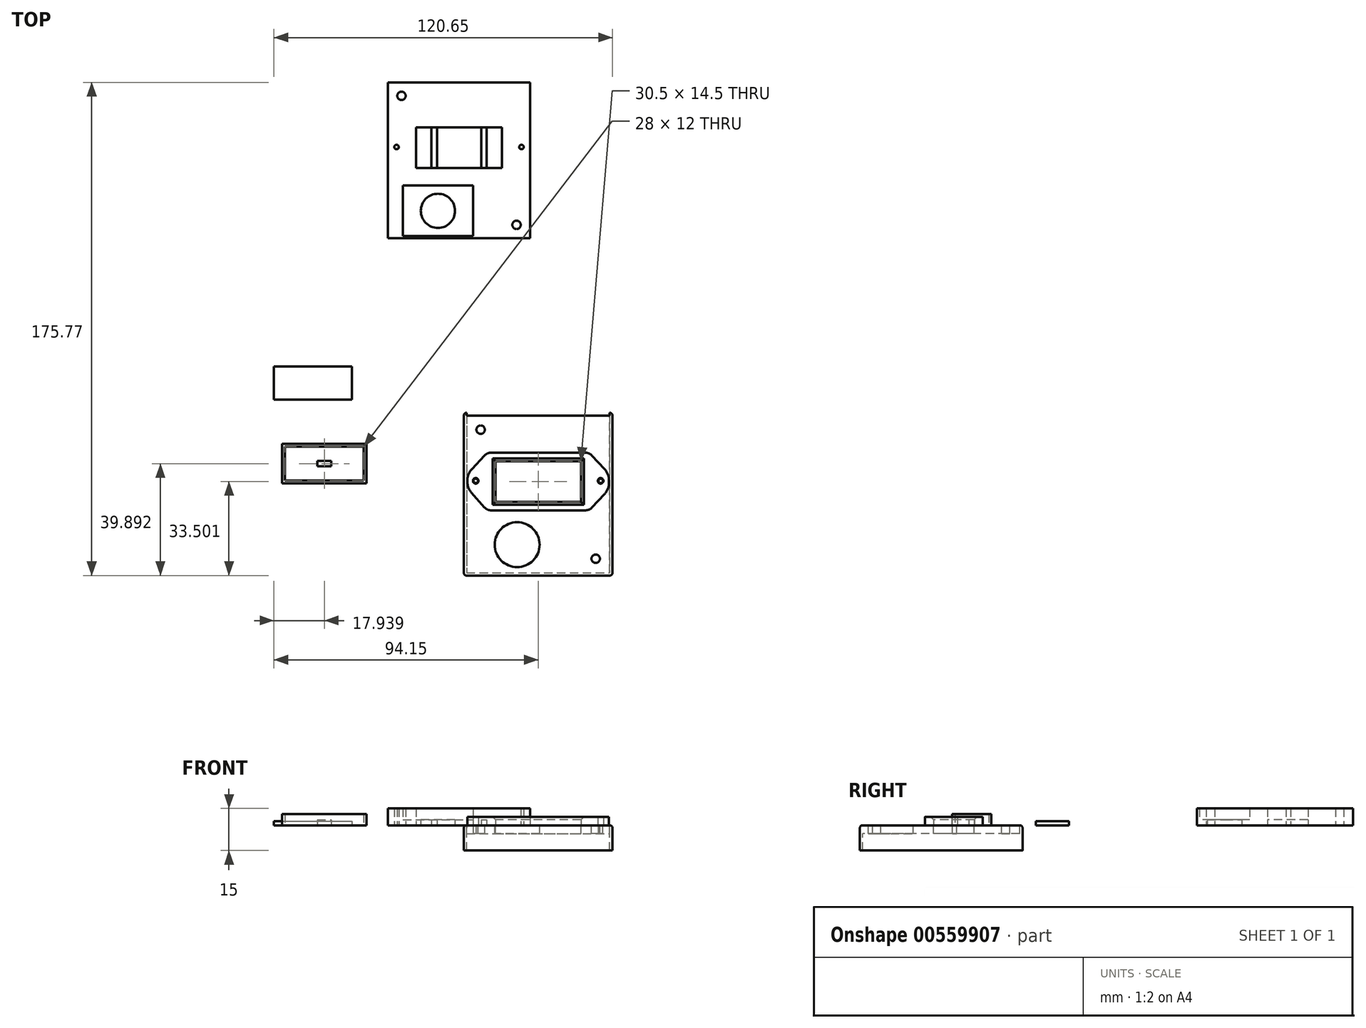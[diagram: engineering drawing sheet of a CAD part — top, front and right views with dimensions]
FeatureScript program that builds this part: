
annotation { "Feature Type Name" : "Feature", "Feature Type Description" : "" }
export const myFeature = defineFeature(function(context is Context, id is Id, definition is map)
    precondition{}
    {
        {
            var Q0;
            Q0=qCreatedBy(makeId("Top.planeOp"),FACE);
            var sketch = newSketch(context, id + "F0", { "sketchPlane" : qUnion([Q0])});
            skLineSegment(sketch, "E0.bottom", {"start": v(25.5, 28) * mm, "end": v(-25.5, 28) * mm});
            skLineSegment(sketch, "E0.top", {"start": v(25.5, -28) * mm, "end": v(-25.5, -28) * mm});
            skLineSegment(sketch, "E0.left", {"start": v(25.5, 28) * mm, "end": v(25.5, -28) * mm});
            skLineSegment(sketch, "E0.right", {"start": v(-25.5, 28) * mm, "end": v(-25.5, -28) * mm});
            skCircle(sketch, "E1", {"center": v(-20.5, 23) * mm, "radius": 1.5 * mm});
            skCircle(sketch, "E2", {"center": v(20.5, -23) * mm, "radius": 1.5 * mm});
            skCircle(sketch, "E3", {"center": v(-7.5, -18) * mm, "radius": 6.1 * mm});
            skLineSegment(sketch, "E4.bottom", {"start": v(-15.25, 11.75) * mm, "end": v(15.25, 11.75) * mm});
            skLineSegment(sketch, "E4.top", {"start": v(-15.25, -2.75) * mm, "end": v(15.25, -2.75) * mm});
            skLineSegment(sketch, "E4.left", {"start": v(-15.25, 11.75) * mm, "end": v(-15.25, -2.75) * mm});
            skLineSegment(sketch, "E4.right", {"start": v(15.25, 11.75) * mm, "end": v(15.25, -2.75) * mm});
            skLineSegment(sketch, "E5.bottom", {"start": v(-2.5, 11.75) * mm, "end": v(2.5, 11.75) * mm});
            skLineSegment(sketch, "E5.top", {"start": v(-2.5, -2.75) * mm, "end": v(2.5, -2.75) * mm});
            skLineSegment(sketch, "E5.left", {"start": v(-2.5, 11.75) * mm, "end": v(-2.5, -2.75) * mm});
            skLineSegment(sketch, "E5.right", {"start": v(2.5, 11.75) * mm, "end": v(2.5, -2.75) * mm});
            skLineSegment(sketch, "E6.bottom", {"start": v(-6.25, 10.5) * mm, "end": v(5.75, 10.5) * mm, "construction": true});
            skLineSegment(sketch, "E6.top", {"start": v(-6.25, -1.5) * mm, "end": v(5.75, -1.5) * mm, "construction": true});
            skLineSegment(sketch, "E6.left", {"start": v(-6.25, 10.5) * mm, "end": v(-6.25, -1.5) * mm, "construction": true});
            skLineSegment(sketch, "E6.right", {"start": v(5.75, 10.5) * mm, "end": v(5.75, -1.5) * mm, "construction": true});
            skLineSegment(sketch, "E7.bottom", {"start": v(-14, 10.5) * mm, "end": v(14, 10.5) * mm, "construction": true});
            skLineSegment(sketch, "E7.top", {"start": v(-14, -1.5) * mm, "end": v(14, -1.5) * mm, "construction": true});
            skLineSegment(sketch, "E7.left", {"start": v(-14, 10.5) * mm, "end": v(-14, -1.5) * mm, "construction": true});
            skLineSegment(sketch, "E7.right", {"start": v(14, 10.5) * mm, "end": v(14, -1.5) * mm, "construction": true});
            skSolve(sketch);
        }
        {
            var Q0;
            Q0=makeQuery(id+"F0.imprint","IMPRINT",FACE,{"disambiguationData":[TD([[makeQuery(id+"F0.imprint","IMPRINT",EDGE,{"derivedFrom":sQuery(id+"F0.wireOp",EDGE,"E0.bottom")}),1.0]])]});
            var Q1;
            Q1=makeQuery(id+"F0.imprint","IMPRINT",FACE,{"disambiguationData":[TD([[makeQuery(id+"F0.imprint","IMPRINT",EDGE,{"derivedFrom":sQuery(id+"F0.wireOp",EDGE,"LN2d2Qam-zQ4N-hJWI-jsZm-hQ2YjQqxJFMe.bottom")}),-1.0]])]});
            var Q2;
            Q2=makeQuery(id+"F0.imprint","IMPRINT",FACE,{"disambiguationData":[TD([[makeQuery(id+"F0.imprint","IMPRINT",EDGE,{"derivedFrom":sQuery(id+"F0.wireOp",EDGE,"Tyq8l7xN-NJ6r-rAiC-5Q4v-MCzvgNdMf9WX.bottom")}),-1.0]])]});
            var Q3;
            Q3=makeQuery(id+"F0.imprint","IMPRINT",FACE,{"disambiguationData":[TD([[makeQuery(id+"F0.imprint","IMPRINT",EDGE,{"derivedFrom":sQuery(id+"F0.wireOp",EDGE,"E5.bottom")}),-1.0]])]});
            var Q4;
            {var subQ12=sQuery(id+"F0.wireOp",EDGE,"5e66b00e-83e9-4da4-8626-02964c2a5a3e.left");Q4=makeQuery(id+"F0.imprint","IMPRINT",FACE,{"disambiguationData":[TD([[makeQuery(id+"F0.imprint","IMPRINT",EDGE,{"derivedFrom":subQ12}),-1.0]])]});}
            var Q5;
            Q5=makeQuery(id+"F0.imprint","IMPRINT",FACE,{"disambiguationData":[TD([[makeQuery(id+"F0.imprint","IMPRINT",EDGE,{"derivedFrom":sQuery(id+"F0.wireOp",EDGE,"242b43d6-e01b-45f4-8fda-c560a832d6e8.bottom")}),-1.0]])]});
            var Q6;
            Q6=makeQuery(id+"F0.imprint","IMPRINT",FACE,{"disambiguationData":[TD([[makeQuery(id+"F0.imprint","IMPRINT",EDGE,{"derivedFrom":sQuery(id+"F0.wireOp",EDGE,"c80b9b78-23ee-44ab-b0c4-abc6401d7a6b.bottom")}),-1.0]])]});
            var Q7;
            Q7=makeQuery(id+"F0.imprint","IMPRINT",FACE,{"disambiguationData":[TD([[makeQuery(id+"F0.imprint","IMPRINT",EDGE,{"derivedFrom":sQuery(id+"F0.wireOp",EDGE,"V3zyF6Pa-9TGi-MSfi-dUwD-Oto6uP0OLka4.bottom")}),-1.0]])]});
            extrude(context, id + "F1", {"entities" : qUnion([Q0, Q1, Q2, Q3, Q4, Q5, Q6, Q7]), "depth" : 1 * mm});
        }
        {
            var Q0;
            Q0=qCreatedBy(makeId("Top.planeOp"),FACE);
            var sketch = newSketch(context, id + "F2", { "sketchPlane" : qUnion([Q0])});
            skPoint(sketch, "E8.middle", {"position": v(28.78, -122.02) * mm});
            skLineSegment(sketch, "E9.bottom", {"start": v(14.21, -108.47) * mm, "end": v(42.21, -108.47) * mm, "construction": true});
            skLineSegment(sketch, "E9.top", {"start": v(14.21, -120.47) * mm, "end": v(42.21, -120.47) * mm, "construction": true});
            skLineSegment(sketch, "E9.left", {"start": v(14.21, -108.47) * mm, "end": v(14.21, -120.47) * mm, "construction": true});
            skLineSegment(sketch, "E9.right", {"start": v(42.21, -108.47) * mm, "end": v(42.21, -120.47) * mm, "construction": true});
            skLineSegment(sketch, "E10.bottom", {"start": v(20.96, -108.47) * mm, "end": v(23.46, -108.47) * mm, "construction": true});
            skLineSegment(sketch, "E10.top", {"start": v(20.96, -120.47) * mm, "end": v(23.46, -120.47) * mm, "construction": true});
            skLineSegment(sketch, "E10.left", {"start": v(20.96, -108.47) * mm, "end": v(20.96, -120.47) * mm, "construction": true});
            skLineSegment(sketch, "E10.right", {"start": v(23.46, -108.47) * mm, "end": v(23.46, -120.47) * mm, "construction": true});
            skLineSegment(sketch, "E11.bottom", {"start": v(32.96, -108.47) * mm, "end": v(35.46, -108.47) * mm, "construction": true});
            skLineSegment(sketch, "E11.top", {"start": v(32.96, -120.47) * mm, "end": v(35.46, -120.47) * mm, "construction": true});
            skLineSegment(sketch, "E11.left", {"start": v(32.96, -108.47) * mm, "end": v(32.96, -120.47) * mm, "construction": true});
            skLineSegment(sketch, "E11.right", {"start": v(35.46, -108.47) * mm, "end": v(35.46, -120.47) * mm, "construction": true});
            skLineSegment(sketch, "E12.bottom", {"start": v(19.21, -111.47) * mm, "end": v(25.21, -111.47) * mm, "construction": true});
            skLineSegment(sketch, "E12.top", {"start": v(19.21, -117.47) * mm, "end": v(25.21, -117.47) * mm, "construction": true});
            skLineSegment(sketch, "E12.left", {"start": v(19.21, -111.47) * mm, "end": v(19.21, -117.47) * mm, "construction": true});
            skLineSegment(sketch, "E12.right", {"start": v(25.21, -111.47) * mm, "end": v(25.21, -117.47) * mm, "construction": true});
            skLineSegment(sketch, "E13.bottom", {"start": v(31.21, -111.47) * mm, "end": v(37.21, -111.47) * mm, "construction": true});
            skLineSegment(sketch, "E13.top", {"start": v(31.21, -117.47) * mm, "end": v(37.21, -117.47) * mm, "construction": true});
            skLineSegment(sketch, "E13.left", {"start": v(31.21, -111.47) * mm, "end": v(31.21, -117.47) * mm, "construction": true});
            skLineSegment(sketch, "E13.right", {"start": v(37.21, -111.47) * mm, "end": v(37.21, -117.47) * mm, "construction": true});
            skLineSegment(sketch, "E14.bottom", {"start": v(2.71, -90.97) * mm, "end": v(53.71, -90.97) * mm});
            skLineSegment(sketch, "E14.top", {"start": v(2.71, -146.97) * mm, "end": v(53.71, -146.97) * mm});
            skLineSegment(sketch, "E14.left", {"start": v(2.71, -90.97) * mm, "end": v(2.71, -146.97) * mm});
            skLineSegment(sketch, "E14.right", {"start": v(53.71, -90.97) * mm, "end": v(53.71, -146.97) * mm});
            skCircle(sketch, "E15", {"center": v(7.71, -95.97) * mm, "radius": 1.5 * mm});
            skCircle(sketch, "E16", {"center": v(48.71, -141.97) * mm, "radius": 1.5 * mm});
            skCircle(sketch, "E17", {"center": v(20.71, -136.97) * mm, "radius": 8 * mm});
            skLineSegment(sketch, "E18.bottom", {"start": v(12.96, -107.22) * mm, "end": v(43.46, -107.22) * mm});
            skLineSegment(sketch, "E18.top", {"start": v(12.96, -121.72) * mm, "end": v(43.46, -121.72) * mm});
            skLineSegment(sketch, "E18.left", {"start": v(12.96, -107.22) * mm, "end": v(12.96, -121.72) * mm});
            skLineSegment(sketch, "E18.right", {"start": v(43.46, -107.22) * mm, "end": v(43.46, -121.72) * mm});
            skPoint(sketch, "E19.middle", {"position": v(-49.22, -118.43) * mm});
            skLineSegment(sketch, "E20.bottom", {"start": v(-62, -102.08) * mm, "end": v(-34, -102.08) * mm});
            skLineSegment(sketch, "E20.top", {"start": v(-62, -114.08) * mm, "end": v(-34, -114.08) * mm});
            skLineSegment(sketch, "E20.left", {"start": v(-62, -102.08) * mm, "end": v(-62, -114.08) * mm});
            skLineSegment(sketch, "E20.right", {"start": v(-34, -102.08) * mm, "end": v(-34, -114.08) * mm});
            skLineSegment(sketch, "E21.bottom", {"start": v(-54.75, -102.08) * mm, "end": v(-52.25, -102.08) * mm, "construction": true});
            skLineSegment(sketch, "E21.top", {"start": v(-54.75, -114.08) * mm, "end": v(-52.25, -114.08) * mm, "construction": true});
            skLineSegment(sketch, "E21.left", {"start": v(-54.75, -102.08) * mm, "end": v(-54.75, -114.08) * mm, "construction": true});
            skLineSegment(sketch, "E21.right", {"start": v(-52.25, -102.08) * mm, "end": v(-52.25, -114.08) * mm, "construction": true});
            skLineSegment(sketch, "E22.bottom", {"start": v(-43.75, -102.08) * mm, "end": v(-41.25, -102.08) * mm, "construction": true});
            skLineSegment(sketch, "E22.top", {"start": v(-43.75, -114.08) * mm, "end": v(-41.25, -114.08) * mm, "construction": true});
            skLineSegment(sketch, "E22.left", {"start": v(-43.75, -102.08) * mm, "end": v(-43.75, -114.08) * mm, "construction": true});
            skLineSegment(sketch, "E22.right", {"start": v(-41.25, -102.08) * mm, "end": v(-41.25, -114.08) * mm, "construction": true});
            skLineSegment(sketch, "E23.bottom", {"start": v(-56.5, -105.08) * mm, "end": v(-50.5, -105.08) * mm, "construction": true});
            skLineSegment(sketch, "E23.top", {"start": v(-56.5, -111.08) * mm, "end": v(-50.5, -111.08) * mm, "construction": true});
            skLineSegment(sketch, "E23.left", {"start": v(-56.5, -105.08) * mm, "end": v(-56.5, -111.08) * mm, "construction": true});
            skLineSegment(sketch, "E23.right", {"start": v(-50.5, -105.08) * mm, "end": v(-50.5, -111.08) * mm, "construction": true});
            skLineSegment(sketch, "E24.bottom", {"start": v(-45.5, -105.08) * mm, "end": v(-39.5, -105.08) * mm, "construction": true});
            skLineSegment(sketch, "E24.top", {"start": v(-45.5, -111.08) * mm, "end": v(-39.5, -111.08) * mm, "construction": true});
            skLineSegment(sketch, "E24.left", {"start": v(-45.5, -105.08) * mm, "end": v(-45.5, -111.08) * mm, "construction": true});
            skLineSegment(sketch, "E24.right", {"start": v(-39.5, -105.08) * mm, "end": v(-39.5, -111.08) * mm, "construction": true});
            skLineSegment(sketch, "E25.bottom", {"start": v(-63, -101.08) * mm, "end": v(-33, -101.08) * mm});
            skLineSegment(sketch, "E25.top", {"start": v(-63, -115.08) * mm, "end": v(-33, -115.08) * mm});
            skLineSegment(sketch, "E25.left", {"start": v(-63, -101.08) * mm, "end": v(-63, -115.08) * mm});
            skLineSegment(sketch, "E25.right", {"start": v(-33, -101.08) * mm, "end": v(-33, -115.08) * mm});
            skLineSegment(sketch, "E26.bottom", {"start": v(-50.5, -107.08) * mm, "end": v(-45.5, -107.08) * mm});
            skLineSegment(sketch, "E26.right", {"start": v(-34, -107.08) * mm, "end": v(-34, -109.08) * mm});
            skLineSegment(sketch, "E27.bottom", {"start": v(-50.5, -102.08) * mm, "end": v(-45.5, -102.08) * mm});
            skLineSegment(sketch, "E27.top", {"start": v(-50.5, -114.08) * mm, "end": v(-45.5, -114.08) * mm});
            skLineSegment(sketch, "E27.left", {"start": v(-50.5, -102.08) * mm, "end": v(-50.5, -114.08) * mm});
            skLineSegment(sketch, "E27.right", {"start": v(-45.5, -102.08) * mm, "end": v(-45.5, -114.08) * mm});
            skLineSegment(sketch, "E28.top", {"start": v(2.71, -89.97) * mm, "end": v(53.71, -89.97) * mm});
            skLineSegment(sketch, "E28.left", {"start": v(2.71, -90.97) * mm, "end": v(2.71, -89.97) * mm});
            skLineSegment(sketch, "E28.right", {"start": v(53.71, -90.97) * mm, "end": v(53.71, -89.97) * mm});
            skLineSegment(sketch, "E29.top", {"start": v(2.71, -147.97) * mm, "end": v(53.71, -147.97) * mm});
            skLineSegment(sketch, "E29.left", {"start": v(2.71, -146.97) * mm, "end": v(2.71, -147.97) * mm});
            skLineSegment(sketch, "E29.right", {"start": v(53.71, -146.97) * mm, "end": v(53.71, -147.97) * mm});
            skLineSegment(sketch, "E30.bottom", {"start": v(53.71, -89.97) * mm, "end": v(54.71, -89.97) * mm});
            skLineSegment(sketch, "E30.top", {"start": v(53.71, -147.97) * mm, "end": v(54.71, -147.97) * mm});
            skLineSegment(sketch, "E30.left", {"start": v(53.71, -89.97) * mm, "end": v(53.71, -147.97) * mm});
            skLineSegment(sketch, "E30.right", {"start": v(54.71, -89.97) * mm, "end": v(54.71, -147.97) * mm});
            skLineSegment(sketch, "E31.bottom", {"start": v(2.71, -89.97) * mm, "end": v(1.71, -89.97) * mm});
            skLineSegment(sketch, "E31.top", {"start": v(2.71, -147.97) * mm, "end": v(1.71, -147.97) * mm});
            skLineSegment(sketch, "E31.left", {"start": v(2.71, -89.97) * mm, "end": v(2.71, -147.97) * mm});
            skLineSegment(sketch, "E31.right", {"start": v(1.71, -89.97) * mm, "end": v(1.71, -147.97) * mm});
            skCircle(sketch, "E32", {"center": v(5.96, -114.22) * mm, "radius": 0.8 * mm});
            skCircle(sketch, "E33", {"center": v(50.46, -114.22) * mm, "radius": 0.8 * mm});
            skLineSegment(sketch, "E34.trimOffspring", {"start": v(-50.5, -109.08) * mm, "end": v(-45.5, -109.08) * mm});
            skSolve(sketch);
        }
        {
            var Q0;
            Q0=qCreatedBy(makeId("Top.planeOp"),FACE);
            var sketch = newSketch(context, id + "F3", { "sketchPlane" : qUnion([Q0])});
            skLineSegment(sketch, "E35.bottom", {"start": v(-65.94, -73.47) * mm, "end": v(-38.14, -73.47) * mm});
            skLineSegment(sketch, "E35.top", {"start": v(-65.94, -85.27) * mm, "end": v(-38.14, -85.27) * mm});
            skLineSegment(sketch, "E35.left", {"start": v(-65.94, -73.47) * mm, "end": v(-65.94, -85.27) * mm});
            skLineSegment(sketch, "E35.right", {"start": v(-38.14, -73.47) * mm, "end": v(-38.14, -85.27) * mm});
            skSolve(sketch);
        }
        {
            var Q0;
            Q0=makeQuery(id+"F1.opExtrude","CAP_FACE",FACE,{"disambiguationData":[OSD([sQuery(id+"F0.wireOp",EDGE,"E0.bottom"),sQuery(id+"F0.wireOp",EDGE,"E0.top"),sQuery(id+"F0.wireOp",EDGE,"E0.left"),sQuery(id+"F0.wireOp",EDGE,"E0.right"),sQuery(id+"F0.wireOp",EDGE,"E1"),sQuery(id+"F0.wireOp",EDGE,"E2"),sQuery(id+"F0.wireOp",EDGE,"E3"),sQuery(id+"F0.wireOp",EDGE,"E4.bottom"),sQuery(id+"F0.wireOp",EDGE,"E4.top"),sQuery(id+"F0.wireOp",EDGE,"E4.left"),sQuery(id+"F0.wireOp",EDGE,"E4.right"),sQuery(id+"F0.wireOp",EDGE,"E5.left"),sQuery(id+"F0.wireOp",EDGE,"E5.right")])],"isStart":false});
            var sketch = newSketch(context, id + "F4", { "sketchPlane" : qUnion([Q0])});
            skLineSegment(sketch, "E36.bottom", {"start": v(-6.25, 10.25) * mm, "end": v(5.75, 10.25) * mm, "construction": true});
            skLineSegment(sketch, "E36.top", {"start": v(-6.25, -1.75) * mm, "end": v(5.75, -1.75) * mm, "construction": true});
            skLineSegment(sketch, "E36.left", {"start": v(-6.25, 10.25) * mm, "end": v(-6.25, -1.75) * mm, "construction": true});
            skLineSegment(sketch, "E36.right", {"start": v(5.75, 10.25) * mm, "end": v(5.75, -1.75) * mm, "construction": true});
            skSolve(sketch);
        }
        {
            var Q0;
            {var subQ3=sQuery(id+"F2.wireOp",EDGE,"E20.left");Q0=makeQuery(id+"F2.imprint","IMPRINT",FACE,{"disambiguationData":[TD([[makeQuery(id+"F2.imprint","IMPRINT",EDGE,{"derivedFrom":subQ3}),-1.0]])]});}
            extrude(context, id + "F5", {"entities" : qUnion([Q0]), "depth" : 4 * mm});
        }
        {
            var Q0;
            Q0=makeQuery(id+"F2.imprint","IMPRINT",FACE,{"disambiguationData":[TD([[makeQuery(id+"F2.imprint","IMPRINT",EDGE,{"derivedFrom":sQuery(id+"F2.wireOp",EDGE,"E15")}),-1.0]])]});
            extrude(context, id + "F6", {"entities" : qUnion([Q0]), "oppositeDirection" : true, "depth" : 3 * mm});
        }
        {
            var Q0;
            Q0=makeQuery(id+"F2.imprint","IMPRINT",FACE,{"disambiguationData":[TD([[makeQuery(id+"F2.imprint","IMPRINT",EDGE,{"derivedFrom":sQuery(id+"F2.wireOp",EDGE,"E26.bottom")}),-1.0]])]});
            var Q1;
            {var subQ5=sQuery(id+"F2.wireOp",EDGE,"E27.bottom");Q1=makeQuery(id+"F2.imprint","IMPRINT",FACE,{"disambiguationData":[TD([[makeQuery(id+"F2.imprint","IMPRINT",EDGE,{"derivedFrom":subQ5}),-1.0]])]});}
            var Q2;
            {var subQ5=sQuery(id+"F2.wireOp",EDGE,"E27.top");Q2=makeQuery(id+"F2.imprint","IMPRINT",FACE,{"disambiguationData":[TD([[makeQuery(id+"F2.imprint","IMPRINT",EDGE,{"derivedFrom":subQ5}),1.0]])]});}
            extrude(context, id + "F7", {"entities" : qUnion([Q0, Q1, Q2]), "operationType" : NewBodyOperationType.ADD, "depth" : 2 * mm});
        }
        {
            var Q0;
            Q0=makeQuery(id+"F3.imprint","IMPRINT",FACE,{"disambiguationData":[TD([[makeQuery(id+"F3.imprint","IMPRINT",EDGE,{"derivedFrom":sQuery(id+"F3.wireOp",EDGE,"E35.bottom")}),-1.0]])]});
            extrude(context, id + "F8", {"entities" : qUnion([Q0]), "depth" : 1.5 * mm});
        }
        {
            var Q0;
            {var subQ3=sQuery(id+"F2.wireOp",EDGE,"E31.bottom");Q0=makeQuery(id+"F2.imprint","IMPRINT",FACE,{"disambiguationData":[TD([[makeQuery(id+"F2.imprint","IMPRINT",EDGE,{"derivedFrom":subQ3}),1.0]])]});}
            var Q1;
            {var subQ0=sQuery(id+"F2.wireOp",EDGE,"E14.bottom");Q1=makeQuery(id+"F2.imprint","IMPRINT",FACE,{"disambiguationData":[TD([[makeQuery(id+"F2.imprint","IMPRINT",EDGE,{"derivedFrom":subQ0}),1.0]])]});}
            var Q2;
            {var subQ0=sQuery(id+"F2.wireOp",EDGE,"E14.top");Q2=makeQuery(id+"F2.imprint","IMPRINT",FACE,{"disambiguationData":[TD([[makeQuery(id+"F2.imprint","IMPRINT",EDGE,{"derivedFrom":subQ0}),-1.0]])]});}
            var Q3;
            {var subQ3=sQuery(id+"F2.wireOp",EDGE,"E30.bottom");Q3=makeQuery(id+"F2.imprint","IMPRINT",FACE,{"disambiguationData":[TD([[makeQuery(id+"F2.imprint","IMPRINT",EDGE,{"derivedFrom":subQ3}),-1.0]])]});}
            extrude(context, id + "F9", {"entities" : qUnion([Q0, Q1, Q2, Q3]), "operationType" : NewBodyOperationType.ADD, "oppositeDirection" : true, "depth" : 9 * mm});
        }
        {
            var Q0;
            Q0=makeQuery(id+"F2.imprint","IMPRINT",FACE,{"disambiguationData":[TD([[makeQuery(id+"F2.imprint","IMPRINT",EDGE,{"derivedFrom":sQuery(id+"F2.wireOp",EDGE,"E15")}),-1.0]])]});
            var sketch = newSketch(context, id + "F10", { "sketchPlane" : qUnion([Q0])});
            skLineSegment(sketch, "E37.bottom", {"start": v(9.96, -104.22) * mm, "end": v(46.46, -104.22) * mm});
            skLineSegment(sketch, "E37.top", {"start": v(9.96, -124.72) * mm, "end": v(46.46, -124.72) * mm});
            skLineSegment(sketch, "E37.left", {"start": v(9.96, -104.22) * mm, "end": v(9.96, -124.72) * mm});
            skLineSegment(sketch, "E37.right", {"start": v(46.46, -104.22) * mm, "end": v(46.46, -124.72) * mm});
            skLineSegment(sketch, "E38", {"start": v(9.96, -124.72) * mm, "end": v(2.96, -116.72) * mm});
            skLineSegment(sketch, "E39", {"start": v(2.96, -116.72) * mm, "end": v(2.96, -111.72) * mm});
            skLineSegment(sketch, "E40", {"start": v(2.96, -111.72) * mm, "end": v(9.96, -104.22) * mm});
            skCircle(sketch, "E41", {"center": v(5.96, -114.22) * mm, "radius": 1 * mm});
            skLineSegment(sketch, "E42.bottom", {"start": v(12.96, -107.22) * mm, "end": v(43.46, -107.22) * mm});
            skLineSegment(sketch, "E42.top", {"start": v(12.96, -121.72) * mm, "end": v(43.46, -121.72) * mm});
            skLineSegment(sketch, "E42.left", {"start": v(12.96, -107.22) * mm, "end": v(12.96, -121.72) * mm});
            skLineSegment(sketch, "E42.right", {"start": v(43.46, -107.22) * mm, "end": v(43.46, -121.72) * mm});
            skLineSegment(sketch, "E43", {"start": v(46.46, -104.22) * mm, "end": v(53.46, -111.72) * mm});
            skLineSegment(sketch, "E44", {"start": v(53.46, -111.72) * mm, "end": v(53.46, -117.22) * mm});
            skLineSegment(sketch, "E45", {"start": v(53.46, -117.22) * mm, "end": v(46.46, -124.72) * mm});
            skCircle(sketch, "E46", {"center": v(50.46, -114.22) * mm, "radius": 1 * mm});
            skSolve(sketch);
        }
        {
            var Q0;
            Q0=qSketchRegion(id+"F10",true);
            extrude(context, id + "F11", {"entities" : qUnion([Q0]), "depth" : 3 * mm});
        }
        {
            var Q0;
            Q0=makeQuery(id+"F11.opExtrude","SWEPT_EDGE",EDGE,{"disambiguationData":[OSD([sQuery(id+"F10.wireOp",EDGE,"E39"),sQuery(id+"F10.wireOp",EDGE,"E40")])]});
            var Q1;
            Q1=makeQuery(id+"F11.opExtrude","SWEPT_EDGE",EDGE,{"disambiguationData":[OSD([sQuery(id+"F10.wireOp",EDGE,"E38"),sQuery(id+"F10.wireOp",EDGE,"E39")])]});
            var Q2;
            Q2=makeQuery(id+"F11.opExtrude","SWEPT_EDGE",EDGE,{"disambiguationData":[OSD([sQuery(id+"F10.wireOp",EDGE,"E44"),sQuery(id+"F10.wireOp",EDGE,"E45")])]});
            var Q3;
            Q3=makeQuery(id+"F11.opExtrude","SWEPT_EDGE",EDGE,{"disambiguationData":[OSD([sQuery(id+"F10.wireOp",EDGE,"E43"),sQuery(id+"F10.wireOp",EDGE,"E44")])]});
            fillet(context, id + "F12", {"entities" : qUnion([Q0, Q1, Q2, Q3]), "radius" : 6 * mm, "tangentPropagation" : true, "allowEdgeOverflow" : false});
        }
        {
            var Q0;
            Q0=makeQuery(id+"F11.opExtrude","SWEPT_EDGE",EDGE,{"disambiguationData":[OSD([sQuery(id+"F10.wireOp",EDGE,"E37.bottom"),sQuery(id+"F10.wireOp",EDGE,"E37.left"),sQuery(id+"F10.wireOp",EDGE,"E40")])]});
            var Q1;
            Q1=makeQuery(id+"F11.opExtrude","SWEPT_EDGE",EDGE,{"disambiguationData":[OSD([sQuery(id+"F10.wireOp",EDGE,"E37.top"),sQuery(id+"F10.wireOp",EDGE,"E37.left"),sQuery(id+"F10.wireOp",EDGE,"E38")])]});
            var Q2;
            Q2=makeQuery(id+"F11.opExtrude","SWEPT_EDGE",EDGE,{"disambiguationData":[OSD([sQuery(id+"F10.wireOp",EDGE,"E37.top"),sQuery(id+"F10.wireOp",EDGE,"E37.right"),sQuery(id+"F10.wireOp",EDGE,"E45")])]});
            var Q3;
            Q3=makeQuery(id+"F11.opExtrude","SWEPT_EDGE",EDGE,{"disambiguationData":[OSD([sQuery(id+"F10.wireOp",EDGE,"E37.bottom"),sQuery(id+"F10.wireOp",EDGE,"E37.right"),sQuery(id+"F10.wireOp",EDGE,"E43")])]});
            fillet(context, id + "F13", {"entities" : qUnion([Q0, Q1, Q2, Q3]), "radius" : 3 * mm, "tangentPropagation" : true, "allowEdgeOverflow" : false});
        }
        {
            var Q0;
            Q0=makeQuery(id+"F9.opExtrude","CAP_EDGE",EDGE,{"disambiguationData":[OSD([sQuery(id+"F2.wireOp",EDGE,"E31.right")])],"isStart":true});
            var Q1;
            Q1=makeQuery(id+"F9.opExtrude","CAP_EDGE",EDGE,{"disambiguationData":[OSD([sQuery(id+"F2.wireOp",EDGE,"E28.top"),sQuery(id+"F2.wireOp",EDGE,"E30.bottom"),sQuery(id+"F2.wireOp",EDGE,"E31.bottom")])],"isStart":true});
            var Q2;
            Q2=makeQuery(id+"F9.opExtrude","CAP_EDGE",EDGE,{"disambiguationData":[OSD([sQuery(id+"F2.wireOp",EDGE,"E29.top"),sQuery(id+"F2.wireOp",EDGE,"E30.top"),sQuery(id+"F2.wireOp",EDGE,"E31.top")])],"isStart":true});
            var Q3;
            Q3=makeQuery(id+"F9.opExtrude","CAP_EDGE",EDGE,{"disambiguationData":[OSD([sQuery(id+"F2.wireOp",EDGE,"E30.right")])],"isStart":true});
            var Q4;
            Q4=makeQuery(id+"F9.opExtrude","SWEPT_EDGE",EDGE,{"disambiguationData":[OSD([sQuery(id+"F2.wireOp",EDGE,"E30.top"),sQuery(id+"F2.wireOp",EDGE,"E30.right")])]});
            var Q5;
            Q5=makeQuery(id+"F9.opExtrude","SWEPT_EDGE",EDGE,{"disambiguationData":[OSD([sQuery(id+"F2.wireOp",EDGE,"E31.top"),sQuery(id+"F2.wireOp",EDGE,"E31.right")])]});
            var Q6;
            Q6=makeQuery(id+"F9.opExtrude","SWEPT_EDGE",EDGE,{"disambiguationData":[OSD([sQuery(id+"F2.wireOp",EDGE,"E31.bottom"),sQuery(id+"F2.wireOp",EDGE,"E31.right")])]});
            var Q7;
            Q7=makeQuery(id+"F9.opExtrude","SWEPT_EDGE",EDGE,{"disambiguationData":[OSD([sQuery(id+"F2.wireOp",EDGE,"E30.bottom"),sQuery(id+"F2.wireOp",EDGE,"E30.right")])]});
            fillet(context, id + "F14", {"entities" : qUnion([Q0, Q1, Q2, Q3, Q4, Q5, Q6, Q7]), "radius" : 1 * mm, "tangentPropagation" : true, "allowEdgeOverflow" : false});
        }
        {
            var Q0;
            Q0=makeQuery(id+"F11.opExtrude","CAP_EDGE",EDGE,{"disambiguationData":[OSD([sQuery(id+"F10.wireOp",EDGE,"E42.left")])],"isStart":false});
            var Q1;
            Q1=makeQuery(id+"F11.opExtrude","CAP_EDGE",EDGE,{"disambiguationData":[OSD([sQuery(id+"F10.wireOp",EDGE,"E42.bottom")])],"isStart":false});
            var Q2;
            Q2=makeQuery(id+"F11.opExtrude","CAP_EDGE",EDGE,{"disambiguationData":[OSD([sQuery(id+"F10.wireOp",EDGE,"E42.right")])],"isStart":false});
            var Q3;
            Q3=makeQuery(id+"F11.opExtrude","CAP_EDGE",EDGE,{"disambiguationData":[OSD([sQuery(id+"F10.wireOp",EDGE,"E42.top")])],"isStart":false});
            chamfer(context, id + "F15", {"entities" : qUnion([Q0, Q1, Q2, Q3]), "width" : 1 * mm, "tangentPropagation" : true});
        }
        {
            var Q0;
            Q0=makeQuery(id+"F1.opExtrude","CAP_FACE",FACE,{"disambiguationData":[OSD([sQuery(id+"F0.wireOp",EDGE,"E0.bottom"),sQuery(id+"F0.wireOp",EDGE,"E0.top"),sQuery(id+"F0.wireOp",EDGE,"E0.left"),sQuery(id+"F0.wireOp",EDGE,"E0.right"),sQuery(id+"F0.wireOp",EDGE,"E1"),sQuery(id+"F0.wireOp",EDGE,"E2"),sQuery(id+"F0.wireOp",EDGE,"E3"),sQuery(id+"F0.wireOp",EDGE,"E4.bottom"),sQuery(id+"F0.wireOp",EDGE,"E4.top"),sQuery(id+"F0.wireOp",EDGE,"E4.left"),sQuery(id+"F0.wireOp",EDGE,"E4.right"),sQuery(id+"F0.wireOp",EDGE,"E5.left"),sQuery(id+"F0.wireOp",EDGE,"E5.right")])],"isStart":false});
            var sketch = newSketch(context, id + "F16", { "sketchPlane" : qUnion([Q0])});
            skCircle(sketch, "E47", {"center": v(-20.5, 23) * mm, "radius": 1.5 * mm});
            skCircle(sketch, "E48", {"center": v(20.5, -23) * mm, "radius": 1.5 * mm});
            skCircle(sketch, "E49", {"center": v(-7.5, -18) * mm, "radius": 8.5 * mm, "construction": true});
            skLineSegment(sketch, "E50.bottom", {"start": v(-25.5, 28) * mm, "end": v(25.5, 28) * mm});
            skLineSegment(sketch, "E50.top", {"start": v(-25.5, -28) * mm, "end": v(25.5, -28) * mm});
            skLineSegment(sketch, "E50.left", {"start": v(-25.5, 28) * mm, "end": v(-25.5, -28) * mm});
            skLineSegment(sketch, "E50.right", {"start": v(25.5, 28) * mm, "end": v(25.5, -28) * mm});
            skLineSegment(sketch, "E51.bottom", {"start": v(-15.25, 11.75) * mm, "end": v(15.25, 11.75) * mm});
            skLineSegment(sketch, "E51.top", {"start": v(-15.25, -2.75) * mm, "end": v(15.25, -2.75) * mm});
            skLineSegment(sketch, "E51.left", {"start": v(-15.25, 11.75) * mm, "end": v(-15.25, -2.75) * mm});
            skLineSegment(sketch, "E51.right", {"start": v(15.25, 11.75) * mm, "end": v(15.25, -2.75) * mm});
            skCircle(sketch, "E52", {"center": v(-22.25, 4.75) * mm, "radius": 2 * mm, "construction": true});
            skCircle(sketch, "E53", {"center": v(22.25, 4.75) * mm, "radius": 2 * mm, "construction": true});
            skLineSegment(sketch, "E54.bottom", {"start": v(5, -27) * mm, "end": v(-20, -27) * mm});
            skLineSegment(sketch, "E54.top", {"start": v(5, -9) * mm, "end": v(-20, -9) * mm});
            skLineSegment(sketch, "E54.left", {"start": v(5, -27) * mm, "end": v(5, -9) * mm});
            skLineSegment(sketch, "E54.right", {"start": v(-20, -27) * mm, "end": v(-20, -9) * mm});
            skSolve(sketch);
        }
        {
            var Q0;
            Q0=makeQuery(id+"F5.opExtrude","CAP_FACE",FACE,{"disambiguationData":[OSD([sQuery(id+"F2.wireOp",EDGE,"E20.bottom"),sQuery(id+"F2.wireOp",EDGE,"E20.top"),sQuery(id+"F2.wireOp",EDGE,"E20.left"),sQuery(id+"F2.wireOp",EDGE,"E20.right"),sQuery(id+"F2.wireOp",EDGE,"E25.bottom"),sQuery(id+"F2.wireOp",EDGE,"E25.top"),sQuery(id+"F2.wireOp",EDGE,"E25.left"),sQuery(id+"F2.wireOp",EDGE,"E25.right"),sQuery(id+"F2.wireOp",EDGE,"E26.left"),sQuery(id+"F2.wireOp",EDGE,"E26.right"),sQuery(id+"F2.wireOp",EDGE,"E27.bottom"),sQuery(id+"F2.wireOp",EDGE,"E27.top")])],"isStart":false});
            var sketch = newSketch(context, id + "F17", { "sketchPlane" : qUnion([Q0])});
            skLineSegment(sketch, "E55.bottom", {"start": v(-63, -101.08) * mm, "end": v(-50.5, -101.08) * mm});
            skLineSegment(sketch, "E55.top", {"start": v(-63, -102.08) * mm, "end": v(-50.5, -102.08) * mm});
            skLineSegment(sketch, "E55.left", {"start": v(-63, -101.08) * mm, "end": v(-63, -102.08) * mm});
            skLineSegment(sketch, "E55.right", {"start": v(-50.5, -101.08) * mm, "end": v(-50.5, -102.08) * mm});
            skLineSegment(sketch, "E56.bottom", {"start": v(-63, -102.08) * mm, "end": v(-62, -102.08) * mm});
            skLineSegment(sketch, "E56.top", {"start": v(-63, -115.08) * mm, "end": v(-62, -115.08) * mm});
            skLineSegment(sketch, "E56.left", {"start": v(-63, -102.08) * mm, "end": v(-63, -115.08) * mm});
            skLineSegment(sketch, "E56.right", {"start": v(-62, -102.08) * mm, "end": v(-62, -115.08) * mm});
            skLineSegment(sketch, "E57.bottom", {"start": v(-50.5, -114.08) * mm, "end": v(-62, -114.08) * mm});
            skLineSegment(sketch, "E57.top", {"start": v(-50.5, -115.08) * mm, "end": v(-62, -115.08) * mm});
            skLineSegment(sketch, "E57.left", {"start": v(-50.5, -114.08) * mm, "end": v(-50.5, -115.08) * mm});
            skLineSegment(sketch, "E57.right", {"start": v(-62, -114.08) * mm, "end": v(-62, -115.08) * mm});
            skLineSegment(sketch, "E58.bottom", {"start": v(-33, -101.08) * mm, "end": v(-45.5, -101.08) * mm});
            skLineSegment(sketch, "E58.top", {"start": v(-33, -102.08) * mm, "end": v(-45.5, -102.08) * mm});
            skLineSegment(sketch, "E58.left", {"start": v(-33, -101.08) * mm, "end": v(-33, -102.08) * mm});
            skLineSegment(sketch, "E58.right", {"start": v(-45.5, -101.08) * mm, "end": v(-45.5, -102.08) * mm});
            skLineSegment(sketch, "E59.bottom", {"start": v(-33, -102.08) * mm, "end": v(-34, -102.08) * mm});
            skLineSegment(sketch, "E59.top", {"start": v(-33, -115.08) * mm, "end": v(-34, -115.08) * mm});
            skLineSegment(sketch, "E59.left", {"start": v(-33, -102.08) * mm, "end": v(-33, -115.08) * mm});
            skLineSegment(sketch, "E59.right", {"start": v(-34, -102.08) * mm, "end": v(-34, -115.08) * mm});
            skLineSegment(sketch, "E60.bottom", {"start": v(-45.5, -114.08) * mm, "end": v(-34, -114.08) * mm});
            skLineSegment(sketch, "E60.top", {"start": v(-45.5, -115.08) * mm, "end": v(-34, -115.08) * mm});
            skLineSegment(sketch, "E60.left", {"start": v(-45.5, -114.08) * mm, "end": v(-45.5, -115.08) * mm});
            skLineSegment(sketch, "E60.right", {"start": v(-34, -114.08) * mm, "end": v(-34, -115.08) * mm});
            skSolve(sketch);
        }
        {
            var Q0;
            {var subQ0=sQuery(id+"F0.wireOp",EDGE,"E3");Q0=makeQuery(id+"FKRJtqk0ZjomfcX_7.boolean.opBoolean","SPLIT",FACE,{"disambiguationData":[TD([makeQuery(id+"F1.opExtrude","SWEPT_FACE",FACE,{"disambiguationData":[OSD([subQ0])]})])],"derivedFrom":makeQuery(id+"F1.opExtrude","CAP_FACE",FACE,{"disambiguationData":[OSD([sQuery(id+"F0.wireOp",EDGE,"E0.bottom"),sQuery(id+"F0.wireOp",EDGE,"E0.top"),sQuery(id+"F0.wireOp",EDGE,"E0.left"),sQuery(id+"F0.wireOp",EDGE,"E0.right"),sQuery(id+"F0.wireOp",EDGE,"E1"),sQuery(id+"F0.wireOp",EDGE,"E2"),subQ0,sQuery(id+"F0.wireOp",EDGE,"E4.bottom"),sQuery(id+"F0.wireOp",EDGE,"E4.top"),sQuery(id+"F0.wireOp",EDGE,"E4.left"),sQuery(id+"F0.wireOp",EDGE,"E4.right"),sQuery(id+"F0.wireOp",EDGE,"E5.left"),sQuery(id+"F0.wireOp",EDGE,"E5.right")])],"isStart":false})});}
            extrude(context, id + "F18", {"entities" : qUnion([Q0]), "operationType" : NewBodyOperationType.ADD, "depth" : 1 * mm});
        }
        {
            var Q0;
            Q0=sQuery(id+"F16.wireOp",VERTEX,"E52.center");
            var Q1;
            Q1=sQuery(id+"F16.wireOp",VERTEX,"E53.center");
            var Q2;
            Q2=makeQuery(id+"F1.opExtrude","SWEPT_BODY",BODY,{"disambiguationData":[OSD([sQuery(id+"F0.wireOp",EDGE,"E0.bottom"),sQuery(id+"F0.wireOp",EDGE,"E0.top"),sQuery(id+"F0.wireOp",EDGE,"E0.left"),sQuery(id+"F0.wireOp",EDGE,"E0.right"),sQuery(id+"F0.wireOp",EDGE,"E1"),sQuery(id+"F0.wireOp",EDGE,"E2"),sQuery(id+"F0.wireOp",EDGE,"E3"),sQuery(id+"F0.wireOp",EDGE,"E4.bottom"),sQuery(id+"F0.wireOp",EDGE,"E4.top"),sQuery(id+"F0.wireOp",EDGE,"E4.left"),sQuery(id+"F0.wireOp",EDGE,"E4.right"),sQuery(id+"F0.wireOp",EDGE,"E5.left"),sQuery(id+"F0.wireOp",EDGE,"E5.right")])]});
            hole(context, id + "F19", {"style" : HoleStyle.SIMPLE, "endStyle" : HoleEndStyle.THROUGH, "holeDiameter" : 1.4 * mm, "isTappedThrough" : true, "tappedDepth" : 12 * mm, "tapClearance" : 3, "locations" : qUnion([Q0, Q1]), "scope" : qUnion([Q2])});
        }
        {
            var Q0;
            {var subQ0=sQuery(id+"F2.wireOp",EDGE,"E27.top");var subQ1=sQuery(id+"F2.wireOp",EDGE,"E27.bottom");var subQ2=sQuery(id+"F2.wireOp",EDGE,"E26.right");var subQ3=sQuery(id+"F2.wireOp",EDGE,"E26.left");Q0=makeQuery(id+"F7.boolean.opBoolean","MERGE",FACE,{"derivedFrom":[makeQuery(id+"F5.opExtrude","CAP_FACE",FACE,{"disambiguationData":[OSD([sQuery(id+"F2.wireOp",EDGE,"E20.bottom"),sQuery(id+"F2.wireOp",EDGE,"E20.top"),sQuery(id+"F2.wireOp",EDGE,"E20.left"),sQuery(id+"F2.wireOp",EDGE,"E20.right"),sQuery(id+"F2.wireOp",EDGE,"E25.bottom"),sQuery(id+"F2.wireOp",EDGE,"E25.top"),sQuery(id+"F2.wireOp",EDGE,"E25.left"),sQuery(id+"F2.wireOp",EDGE,"E25.right"),subQ3,subQ2,subQ1,subQ0])],"isStart":true}),makeQuery(id+"F7.opExtrude","CAP_FACE",FACE,{"disambiguationData":[OSD([sQuery(id+"F2.wireOp",EDGE,"E26.bottom"),sQuery(id+"F2.wireOp",EDGE,"E26.top"),subQ3,subQ2,subQ1,subQ0,sQuery(id+"F2.wireOp",EDGE,"E27.left"),sQuery(id+"F2.wireOp",EDGE,"E27.right")])],"isStart":true})]});}
            var sketch = newSketch(context, id + "F20", { "sketchPlane" : qUnion([Q0])});
            skLineSegment(sketch, "E61.bottom", {"start": v(-63, 115.08) * mm, "end": v(-33, 115.08) * mm});
            skLineSegment(sketch, "E61.top", {"start": v(-63, 114.08) * mm, "end": v(-33, 114.08) * mm});
            skLineSegment(sketch, "E61.left", {"start": v(-63, 115.08) * mm, "end": v(-63, 114.08) * mm});
            skLineSegment(sketch, "E61.right", {"start": v(-33, 115.08) * mm, "end": v(-33, 114.08) * mm});
            skLineSegment(sketch, "E62.bottom", {"start": v(-63, 114.08) * mm, "end": v(-62, 114.08) * mm});
            skLineSegment(sketch, "E62.top", {"start": v(-63, 101.08) * mm, "end": v(-62, 101.08) * mm});
            skLineSegment(sketch, "E62.left", {"start": v(-63, 114.08) * mm, "end": v(-63, 101.08) * mm});
            skLineSegment(sketch, "E62.right", {"start": v(-62, 114.08) * mm, "end": v(-62, 101.08) * mm});
            skLineSegment(sketch, "E63.bottom", {"start": v(-62, 101.08) * mm, "end": v(-33, 101.08) * mm});
            skLineSegment(sketch, "E63.top", {"start": v(-62, 102.08) * mm, "end": v(-33, 102.08) * mm});
            skLineSegment(sketch, "E63.left", {"start": v(-62, 101.08) * mm, "end": v(-62, 102.08) * mm});
            skLineSegment(sketch, "E63.right", {"start": v(-33, 101.08) * mm, "end": v(-33, 102.08) * mm});
            skLineSegment(sketch, "E64.bottom", {"start": v(-33, 114.08) * mm, "end": v(-34, 114.08) * mm});
            skLineSegment(sketch, "E64.top", {"start": v(-33, 102.08) * mm, "end": v(-34, 102.08) * mm});
            skLineSegment(sketch, "E64.left", {"start": v(-33, 114.08) * mm, "end": v(-33, 102.08) * mm});
            skLineSegment(sketch, "E64.right", {"start": v(-34, 114.08) * mm, "end": v(-34, 102.08) * mm});
            skSolve(sketch);
        }
        {
            var Q0;
            Q0=sQuery(id+"F16.wireOp",VERTEX,"E52.center");
            var Q1;
            Q1=sQuery(id+"F16.wireOp",VERTEX,"E53.center");
            var Q2;
            Q2=makeQuery(id+"F1.opExtrude","SWEPT_BODY",BODY,{"disambiguationData":[OSD([sQuery(id+"F0.wireOp",EDGE,"E0.bottom"),sQuery(id+"F0.wireOp",EDGE,"E0.top"),sQuery(id+"F0.wireOp",EDGE,"E0.left"),sQuery(id+"F0.wireOp",EDGE,"E0.right"),sQuery(id+"F0.wireOp",EDGE,"E1"),sQuery(id+"F0.wireOp",EDGE,"E2"),sQuery(id+"F0.wireOp",EDGE,"E3"),sQuery(id+"F0.wireOp",EDGE,"E4.bottom"),sQuery(id+"F0.wireOp",EDGE,"E4.top"),sQuery(id+"F0.wireOp",EDGE,"E4.left"),sQuery(id+"F0.wireOp",EDGE,"E4.right"),sQuery(id+"F0.wireOp",EDGE,"E5.left"),sQuery(id+"F0.wireOp",EDGE,"E5.right")])]});
            hole(context, id + "F21", {"style" : HoleStyle.SIMPLE, "endStyle" : HoleEndStyle.THROUGH, "oppositeDirection" : true, "holeDiameter" : 1.4 * mm, "isTappedThrough" : true, "tappedDepth" : 12 * mm, "tapClearance" : 3, "locations" : qUnion([Q0, Q1]), "scope" : qUnion([Q2])});
        }
        {
            var Q0;
            Q0=makeQuery(id+"F16.imprint","IMPRINT",FACE,{"disambiguationData":[TD([[makeQuery(id+"F16.imprint","IMPRINT",EDGE,{"derivedFrom":sQuery(id+"F16.wireOp",EDGE,"E47")}),-1.0]])]});
            extrude(context, id + "F22", {"entities" : qUnion([Q0]), "operationType" : NewBodyOperationType.ADD, "depth" : 5 * mm});
        }
        {
            var Q0;
            Q0=makeQuery(id+"F1.opExtrude","CAP_FACE",FACE,{"disambiguationData":[OSD([sQuery(id+"F0.wireOp",EDGE,"E0.bottom"),sQuery(id+"F0.wireOp",EDGE,"E0.top"),sQuery(id+"F0.wireOp",EDGE,"E0.left"),sQuery(id+"F0.wireOp",EDGE,"E0.right"),sQuery(id+"F0.wireOp",EDGE,"E1"),sQuery(id+"F0.wireOp",EDGE,"E2"),sQuery(id+"F0.wireOp",EDGE,"E3"),sQuery(id+"F0.wireOp",EDGE,"E4.bottom"),sQuery(id+"F0.wireOp",EDGE,"E4.top"),sQuery(id+"F0.wireOp",EDGE,"E4.left"),sQuery(id+"F0.wireOp",EDGE,"E4.right"),sQuery(id+"F0.wireOp",EDGE,"E5.left"),sQuery(id+"F0.wireOp",EDGE,"E5.right")])],"isStart":true});
            var sketch = newSketch(context, id + "F23", { "sketchPlane" : qUnion([Q0])});
            skLineSegment(sketch, "E65.bottom", {"start": v(-25.5, 28) * mm, "end": v(25.5, 28) * mm});
            skLineSegment(sketch, "E65.top", {"start": v(-25.5, 27.8) * mm, "end": v(25.5, 27.8) * mm});
            skLineSegment(sketch, "E65.left", {"start": v(-25.5, 28) * mm, "end": v(-25.5, 27.8) * mm});
            skLineSegment(sketch, "E65.right", {"start": v(25.5, 28) * mm, "end": v(25.5, 27.8) * mm});
            skLineSegment(sketch, "E66.bottom", {"start": v(-25.5, -28) * mm, "end": v(25.5, -28) * mm});
            skLineSegment(sketch, "E66.top", {"start": v(-25.5, -27.8) * mm, "end": v(25.5, -27.8) * mm});
            skLineSegment(sketch, "E66.left", {"start": v(-25.5, -28) * mm, "end": v(-25.5, -27.8) * mm});
            skLineSegment(sketch, "E66.right", {"start": v(25.5, -28) * mm, "end": v(25.5, -27.8) * mm});
            skLineSegment(sketch, "E67.bottom", {"start": v(-25.5, -27.8) * mm, "end": v(-25.3, -27.8) * mm});
            skLineSegment(sketch, "E67.top", {"start": v(-25.5, 27.8) * mm, "end": v(-25.3, 27.8) * mm});
            skLineSegment(sketch, "E67.left", {"start": v(-25.5, -27.8) * mm, "end": v(-25.5, 27.8) * mm});
            skLineSegment(sketch, "E67.right", {"start": v(-25.3, -27.8) * mm, "end": v(-25.3, 27.8) * mm});
            skLineSegment(sketch, "E68.bottom", {"start": v(25.5, -27.8) * mm, "end": v(25.3, -27.8) * mm});
            skLineSegment(sketch, "E68.top", {"start": v(25.5, 27.8) * mm, "end": v(25.3, 27.8) * mm});
            skLineSegment(sketch, "E68.left", {"start": v(25.5, -27.8) * mm, "end": v(25.5, 27.8) * mm});
            skLineSegment(sketch, "E68.right", {"start": v(25.3, -27.8) * mm, "end": v(25.3, 27.8) * mm});
            skSolve(sketch);
        }
        {
            var Q0;
            Q0=qSketchRegion(id+"F23",true);
            extrude(context, id + "F24", {"entities" : qUnion([Q0]), "operationType" : NewBodyOperationType.REMOVE, "oppositeDirection" : true, "depth" : 25 * mm});
        }
        {
            var Q0;
            Q0=sQuery(id+"F16.wireOp",VERTEX,"E52.center");
            var Q1;
            Q1=sQuery(id+"F16.wireOp",VERTEX,"E53.center");
            var Q2;
            Q2=makeQuery(id+"F1.opExtrude","SWEPT_BODY",BODY,{"disambiguationData":[OSD([sQuery(id+"F0.wireOp",EDGE,"E0.bottom"),sQuery(id+"F0.wireOp",EDGE,"E0.top"),sQuery(id+"F0.wireOp",EDGE,"E0.left"),sQuery(id+"F0.wireOp",EDGE,"E0.right"),sQuery(id+"F0.wireOp",EDGE,"E1"),sQuery(id+"F0.wireOp",EDGE,"E2"),sQuery(id+"F0.wireOp",EDGE,"E3"),sQuery(id+"F0.wireOp",EDGE,"E4.bottom"),sQuery(id+"F0.wireOp",EDGE,"E4.top"),sQuery(id+"F0.wireOp",EDGE,"E4.left"),sQuery(id+"F0.wireOp",EDGE,"E4.right"),sQuery(id+"F0.wireOp",EDGE,"E5.left"),sQuery(id+"F0.wireOp",EDGE,"E5.right")])]});
            hole(context, id + "F25", {"style" : HoleStyle.SIMPLE, "endStyle" : HoleEndStyle.THROUGH, "oppositeDirection" : true, "holeDiameter" : 1.6 * mm, "isTappedThrough" : true, "tappedDepth" : 12 * mm, "tapClearance" : 3, "locations" : qUnion([Q0, Q1]), "scope" : qUnion([Q2])});
        }
        {
            var Q0;
            Q0=sQuery(id+"F16.wireOp",VERTEX,"E53.center");
            var Q1;
            Q1=sQuery(id+"F16.wireOp",VERTEX,"E52.center");
            var Q2;
            Q2=makeQuery(id+"F1.opExtrude","SWEPT_BODY",BODY,{"disambiguationData":[OSD([sQuery(id+"F0.wireOp",EDGE,"E0.bottom"),sQuery(id+"F0.wireOp",EDGE,"E0.top"),sQuery(id+"F0.wireOp",EDGE,"E0.left"),sQuery(id+"F0.wireOp",EDGE,"E0.right"),sQuery(id+"F0.wireOp",EDGE,"E1"),sQuery(id+"F0.wireOp",EDGE,"E2"),sQuery(id+"F0.wireOp",EDGE,"E3"),sQuery(id+"F0.wireOp",EDGE,"E4.bottom"),sQuery(id+"F0.wireOp",EDGE,"E4.top"),sQuery(id+"F0.wireOp",EDGE,"E4.left"),sQuery(id+"F0.wireOp",EDGE,"E4.right"),sQuery(id+"F0.wireOp",EDGE,"E5.left"),sQuery(id+"F0.wireOp",EDGE,"E5.right")])]});
            hole(context, id + "F26", {"style" : HoleStyle.SIMPLE, "endStyle" : HoleEndStyle.THROUGH, "holeDiameter" : 1.6 * mm, "isTappedThrough" : true, "tappedDepth" : 12 * mm, "tapClearance" : 3, "locations" : qUnion([Q0, Q1]), "scope" : qUnion([Q2])});
        }
        {
            var Q0;
            Q0=makeQuery(id+"F1.opExtrude","CAP_FACE",FACE,{"disambiguationData":[OSD([sQuery(id+"F0.wireOp",EDGE,"E0.bottom"),sQuery(id+"F0.wireOp",EDGE,"E0.top"),sQuery(id+"F0.wireOp",EDGE,"E0.left"),sQuery(id+"F0.wireOp",EDGE,"E0.right"),sQuery(id+"F0.wireOp",EDGE,"E1"),sQuery(id+"F0.wireOp",EDGE,"E2"),sQuery(id+"F0.wireOp",EDGE,"E3"),sQuery(id+"F0.wireOp",EDGE,"E4.bottom"),sQuery(id+"F0.wireOp",EDGE,"E4.top"),sQuery(id+"F0.wireOp",EDGE,"E4.left"),sQuery(id+"F0.wireOp",EDGE,"E4.right"),sQuery(id+"F0.wireOp",EDGE,"E5.left"),sQuery(id+"F0.wireOp",EDGE,"E5.right")])],"isStart":true});
            var sketch = newSketch(context, id + "F27", { "sketchPlane" : qUnion([Q0])});
            skLineSegment(sketch, "E69.bottom", {"start": v(-9.88, -11.75) * mm, "end": v(-7.88, -11.75) * mm});
            skLineSegment(sketch, "E69.top", {"start": v(-9.88, 2.75) * mm, "end": v(-7.88, 2.75) * mm});
            skLineSegment(sketch, "E69.left", {"start": v(-9.88, -11.75) * mm, "end": v(-9.88, 2.75) * mm});
            skLineSegment(sketch, "E69.right", {"start": v(-7.88, -11.75) * mm, "end": v(-7.88, 2.75) * mm});
            skLineSegment(sketch, "E70.bottom", {"start": v(9.87, 2.75) * mm, "end": v(7.87, 2.75) * mm});
            skLineSegment(sketch, "E70.top", {"start": v(9.88, -11.75) * mm, "end": v(7.88, -11.75) * mm});
            skLineSegment(sketch, "E70.left", {"start": v(9.87, 2.75) * mm, "end": v(9.88, -11.75) * mm});
            skLineSegment(sketch, "E70.right", {"start": v(7.87, 2.75) * mm, "end": v(7.88, -11.75) * mm});
            skSolve(sketch);
        }
        {
            var Q0;
            Q0=makeQuery(id+"F27.imprint","IMPRINT",FACE,{"disambiguationData":[TD([[makeQuery(id+"F27.imprint","IMPRINT",EDGE,{"derivedFrom":sQuery(id+"F27.wireOp",EDGE,"E69.bottom")}),1.0]])]});
            var Q1;
            Q1=makeQuery(id+"F27.imprint","IMPRINT",FACE,{"disambiguationData":[TD([[makeQuery(id+"F27.imprint","IMPRINT",EDGE,{"derivedFrom":sQuery(id+"F27.wireOp",EDGE,"E70.bottom")}),-1.0]])]});
            extrude(context, id + "F28", {"entities" : qUnion([Q0, Q1]), "operationType" : NewBodyOperationType.ADD, "oppositeDirection" : true, "depth" : 2 * mm});
        }
    });
